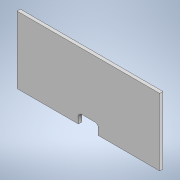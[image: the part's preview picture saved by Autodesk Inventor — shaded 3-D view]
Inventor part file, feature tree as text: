
AUTODESK INVENTOR PART (.ipt)
format: ipt  version: 2021 (Build 250183000, 183)  size: 115,712 bytes
history: native  units: mm
features: extrude x3, sketch x3, fillet x1
ambient origin geometry x8: Origin, YZ Plane, XZ Plane, XY Plane, X Axis, Y Axis, Z Axis, Center Point
bodies: Solid1 (feature_tree)
feature tree (7):
  extrude  "Extrusion1"  Depth=86.0mm
  extrude  "Extrusion2"  Depth=6.0mm
  fillet  "Fillet1"  Radius=12.0mm
  extrude  "Extrusion3"  Depth=86.0mm
  sketch  "Sketch1"  dims[d0=86.0mm d1=42.5mm]
  sketch  "Sketch2"  dims[d2=2.0mm d3=0.0mm d4=6.0mm d5=12.0mm]
  sketch  "Sketch3"  dims[d6=37.0mm d7=86.0mm d8=2.0mm d9=0.0mm d10=2.0mm d11=2.0mm d12=2.0mm d13=0.0mm]
